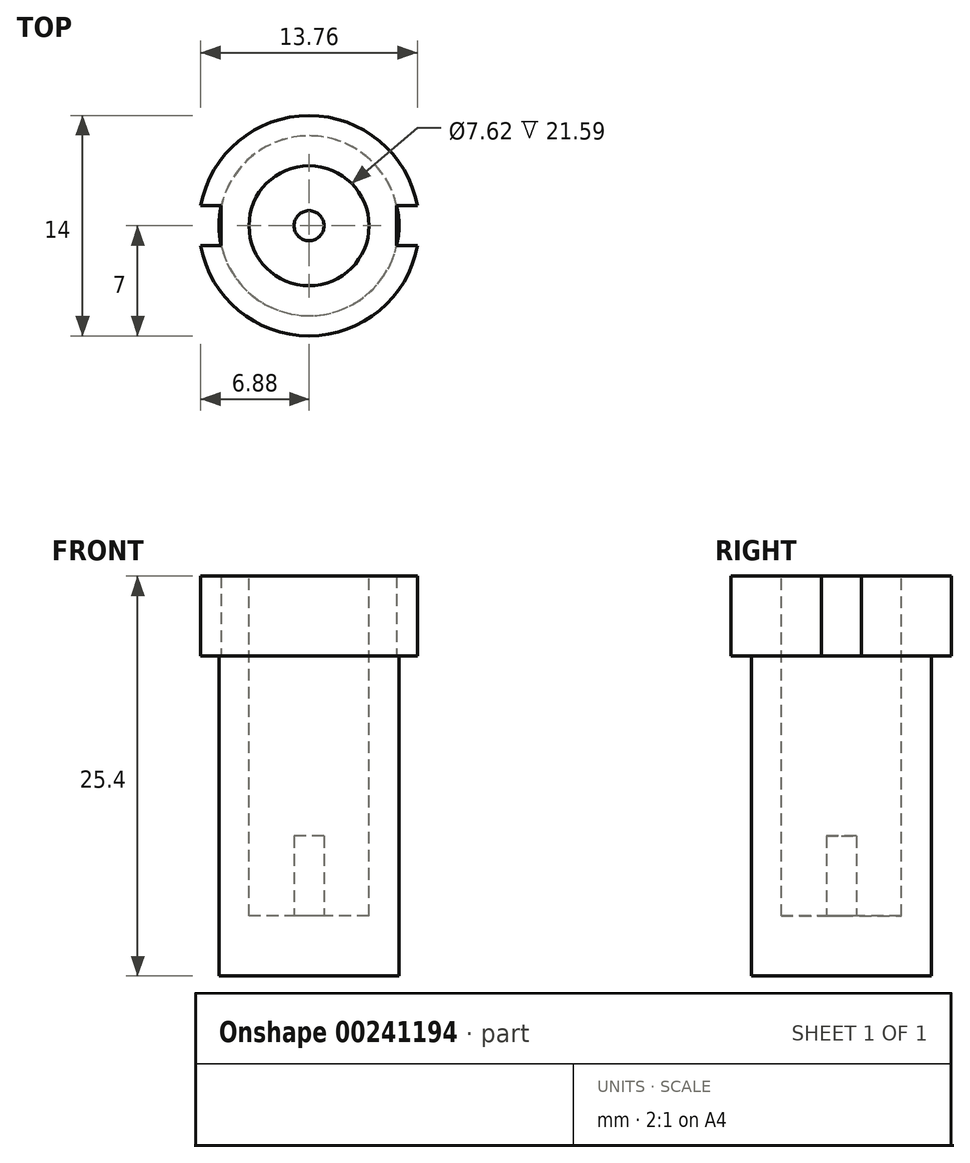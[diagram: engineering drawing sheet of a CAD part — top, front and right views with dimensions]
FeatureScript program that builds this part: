
annotation { "Feature Type Name" : "Feature", "Feature Type Description" : "" }
export const myFeature = defineFeature(function(context is Context, id is Id, definition is map)
    precondition{}
    {
        {
            var Q0;
            Q0=qCreatedBy(makeId("Top.planeOp"),FACE);
            var sketch = newSketch(context, id + "F0", { "sketchPlane" : qUnion([Q0])});
            skCircle(sketch, "E0", {"center": v(0, 0) * mm, "radius": 7 * mm});
            skSolve(sketch);
        }
        {
            var Q0;
            Q0 = qSketchRegion(id + "F0", true);
            extrude(context, id + "F1", {"entities" : qUnion([Q0]), "depth" : 25.4 * mm});
        }
        {
            var Q0;
            Q0=makeQuery(id+"F1.opExtrude","CAP_FACE",FACE,{"disambiguationData":[OSD([sQuery(id+"F0.wireOp",EDGE,"E0")])],"isStart":false});
            var sketch = newSketch(context, id + "F2", { "sketchPlane" : qUnion([Q0])});
            skCircle(sketch, "E1", {"center": v(0, 0) * mm, "radius": 3.81 * mm});
            skSolve(sketch);
        }
        {
            var Q0;
            Q0 = qSketchRegion(id + "F2", true);
            extrude(context, id + "F3", {"entities" : qUnion([Q0]), "operationType" : NewBodyOperationType.REMOVE, "oppositeDirection" : true, "depth" : 21.59 * mm});
        }
        {
            var Q0;
            Q0=makeQuery(id+"F1.opExtrude","CAP_FACE",FACE,{"disambiguationData":[OSD([sQuery(id+"F0.wireOp",EDGE,"E0")])],"isStart":true});
            var sketch = newSketch(context, id + "F4", { "sketchPlane" : qUnion([Q0])});
            skCircle(sketch, "E2", {"center": v(0, 0) * mm, "radius": 5.72 * mm});
            skSolve(sketch);
        }
        {
            var Q0;
            Q0=makeQuery(id+"F4.imprint","IMPRINT",FACE,{"disambiguationData":[TD([[makeQuery(id+"F4.imprint","IMPRINT",EDGE,{"derivedFrom":sQuery(id+"F4.wireOp",EDGE,"E2")}),-1.0]])]});
            extrude(context, id + "F5", {"entities" : qUnion([Q0]), "operationType" : NewBodyOperationType.REMOVE, "oppositeDirection" : true, "depth" : 20.32 * mm});
        }
        {
            var Q0;
            Q0=makeQuery(id+"F5.boolean.opBoolean","COPY",FACE,{"derivedFrom":makeQuery(id+"F5.opExtrude","CAP_FACE",FACE,{"disambiguationData":[OSD([sQuery(id+"F0.wireOp",EDGE,"E0"),sQuery(id+"F4.wireOp",EDGE,"E2")])],"isStart":false})});
            var sketch = newSketch(context, id + "F6", { "sketchPlane" : qUnion([Q0])});
            skLineSegment(sketch, "E3.bottom", {"start": v(5.57, 1.27) * mm, "end": v(8.37, 1.27) * mm});
            skLineSegment(sketch, "E3.top", {"start": v(5.57, -1.27) * mm, "end": v(8.37, -1.27) * mm});
            skLineSegment(sketch, "E3.left", {"start": v(5.57, 1.27) * mm, "end": v(5.57, -1.27) * mm});
            skLineSegment(sketch, "E3.right", {"start": v(8.37, 1.27) * mm, "end": v(8.37, -1.27) * mm});
            skLineSegment(sketch, "E4.MirrorCS", {"start": v(-8.37, 1.27) * mm, "end": v(-8.37, -1.27) * mm});
            skLineSegment(sketch, "E5.MirrorCS", {"start": v(-5.57, 1.27) * mm, "end": v(-8.37, 1.27) * mm});
            skLineSegment(sketch, "E6.MirrorCS", {"start": v(-5.57, -1.27) * mm, "end": v(-8.37, -1.27) * mm});
            skLineSegment(sketch, "E7.MirrorCS", {"start": v(-5.57, 1.27) * mm, "end": v(-5.57, -1.27) * mm});
            skSolve(sketch);
        }
        {
            var Q0;
            Q0 = qSketchRegion(id + "F6", true);
            extrude(context, id + "F7", {"entities" : qUnion([Q0]), "operationType" : NewBodyOperationType.REMOVE, "oppositeDirection" : true, "depth" : 25.4 * mm});
        }
        {
            var Q0;
            Q0=makeQuery(id+"F3.boolean.opBoolean","COPY",FACE,{"derivedFrom":makeQuery(id+"F3.opExtrude","CAP_FACE",FACE,{"disambiguationData":[OSD([sQuery(id+"F2.wireOp",EDGE,"E1")])],"isStart":false})});
            var sketch = newSketch(context, id + "F8", { "sketchPlane" : qUnion([Q0])});
            skCircle(sketch, "E8", {"center": v(0, 0) * mm, "radius": 0.95 * mm});
            skSolve(sketch);
        }
        {
            var Q0;
            Q0 = qSketchRegion(id + "F8", true);
            extrude(context, id + "F9", {"entities" : qUnion([Q0]), "operationType" : NewBodyOperationType.ADD, "depth" : 5.08 * mm});
        }
    });
